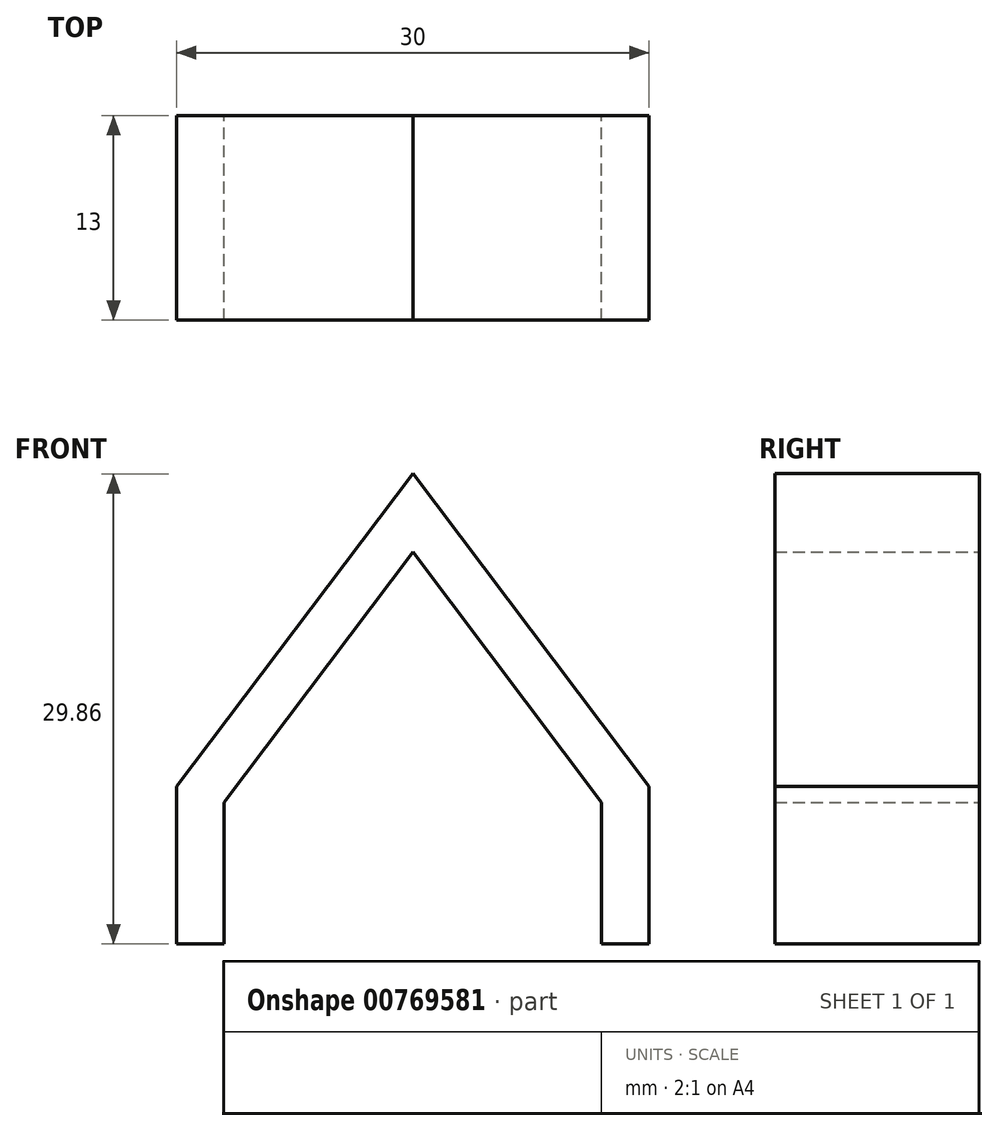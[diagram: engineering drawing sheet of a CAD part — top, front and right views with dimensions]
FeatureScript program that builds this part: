
annotation { "Feature Type Name" : "Feature", "Feature Type Description" : "" }
export const myFeature = defineFeature(function(context is Context, id is Id, definition is map)
    precondition{}
    {
        {
            var Q0;
            Q0=qCreatedBy(makeId("Front.planeOp"),FACE);
            var sketch = newSketch(context, id + "F0", { "sketchPlane" : qUnion([Q0])});
            skLineSegment(sketch, "E0", {"start": v(-15, 0) * mm, "end": v(0, 19.86) * mm});
            skLineSegment(sketch, "E1", {"start": v(0, 19.86) * mm, "end": v(15, 0) * mm});
            skLineSegment(sketch, "E2", {"start": v(15, 0) * mm, "end": v(15, -10) * mm});
            skLineSegment(sketch, "E3", {"start": v(15, -10) * mm, "end": v(-15, -10) * mm});
            skLineSegment(sketch, "E4", {"start": v(-15, -10) * mm, "end": v(-15, 0) * mm});
            skPoint(sketch, "E5", {"position": v(0, 0) * mm});
            skLineSegment(sketch, "E6.0", {"start": v(-12, -1) * mm, "end": v(0, 14.89) * mm});
            skLineSegment(sketch, "E7.0", {"start": v(0, 14.89) * mm, "end": v(12, -1) * mm});
            skLineSegment(sketch, "E8.0", {"start": v(-12, -10) * mm, "end": v(-12, -1) * mm});
            skLineSegment(sketch, "E9.0", {"start": v(12, -1) * mm, "end": v(12, -10) * mm});
            skLineSegment(sketch, "E10", {"start": v(-15, -10) * mm, "end": v(-12, -10) * mm});
            skLineSegment(sketch, "E11", {"start": v(12, -10) * mm, "end": v(15, -10) * mm});
            skPoint(sketch, "E12", {"position": v(0, -1.53) * mm});
            skSolve(sketch);
        }
        {
            var Q0;
            Q0=makeQuery(id+"F0.imprint","IMPRINT",FACE,{"disambiguationData":[TD([[makeQuery(id+"F0.imprint","IMPRINT",EDGE,{"derivedFrom":sQuery(id+"F0.wireOp",EDGE,"E0")}),-1.0]])]});
            extrude(context, id + "F1", {"entities" : qUnion([Q0]), "depth" : 10 * mm, "offsetDistance" : 25 * mm});
        }
        {
            var Q0;
            Q0=makeQuery(id+"F0.imprint","IMPRINT",FACE,{"disambiguationData":[TD([[makeQuery(id+"F0.imprint","IMPRINT",EDGE,{"derivedFrom":sQuery(id+"F0.wireOp",EDGE,"E3")}),-1.0]])]});
            var Q1;
            Q1=makeQuery(id+"F1.opExtrude","CAP_FACE",FACE,{"disambiguationData":[OSD([sQuery(id+"F0.wireOp",EDGE,"E0"),sQuery(id+"F0.wireOp",EDGE,"E1"),sQuery(id+"F0.wireOp",EDGE,"E2"),sQuery(id+"F0.wireOp",EDGE,"E4"),sQuery(id+"F0.wireOp",EDGE,"E6.0"),sQuery(id+"F0.wireOp",EDGE,"E7.0"),sQuery(id+"F0.wireOp",EDGE,"E8.0"),sQuery(id+"F0.wireOp",EDGE,"E9.0"),sQuery(id+"F0.wireOp",EDGE,"E10"),sQuery(id+"F0.wireOp",EDGE,"E11")])],"isStart":false});
            extrude(context, id + "F2", {"entities" : qUnion([Q0, Q1]), "operationType" : NewBodyOperationType.ADD, "depth" : 3 * mm, "offsetDistance" : 25 * mm});
        }
        {
            var Q0;
            Q0=sQuery(id+"F0.wireOp",VERTEX,"E12");
            var Q1;
            Q1=makeQuery(id+"F1.opExtrude","SWEPT_BODY",BODY,{"disambiguationData":[OSD([sQuery(id+"F0.wireOp",EDGE,"E0"),sQuery(id+"F0.wireOp",EDGE,"E1"),sQuery(id+"F0.wireOp",EDGE,"E2"),sQuery(id+"F0.wireOp",EDGE,"E4"),sQuery(id+"F0.wireOp",EDGE,"E6.0"),sQuery(id+"F0.wireOp",EDGE,"E7.0"),sQuery(id+"F0.wireOp",EDGE,"E8.0"),sQuery(id+"F0.wireOp",EDGE,"E9.0"),sQuery(id+"F0.wireOp",EDGE,"E10"),sQuery(id+"F0.wireOp",EDGE,"E11")])]});
            hole(context, id + "F3", {"style" : HoleStyle.SIMPLE, "endStyle" : HoleEndStyle.BLIND, "oppositeDirection" : true, "holeDiameter" : 5 * mm, "majorDiameter" : 5 * mm, "holeDepth" : 12 * mm, "isTappedThrough" : true, "tappedDepth" : 12 * mm, "tapClearance" : 3, "locations" : qUnion([Q0]), "scope" : qUnion([Q1])});
        }
    });
